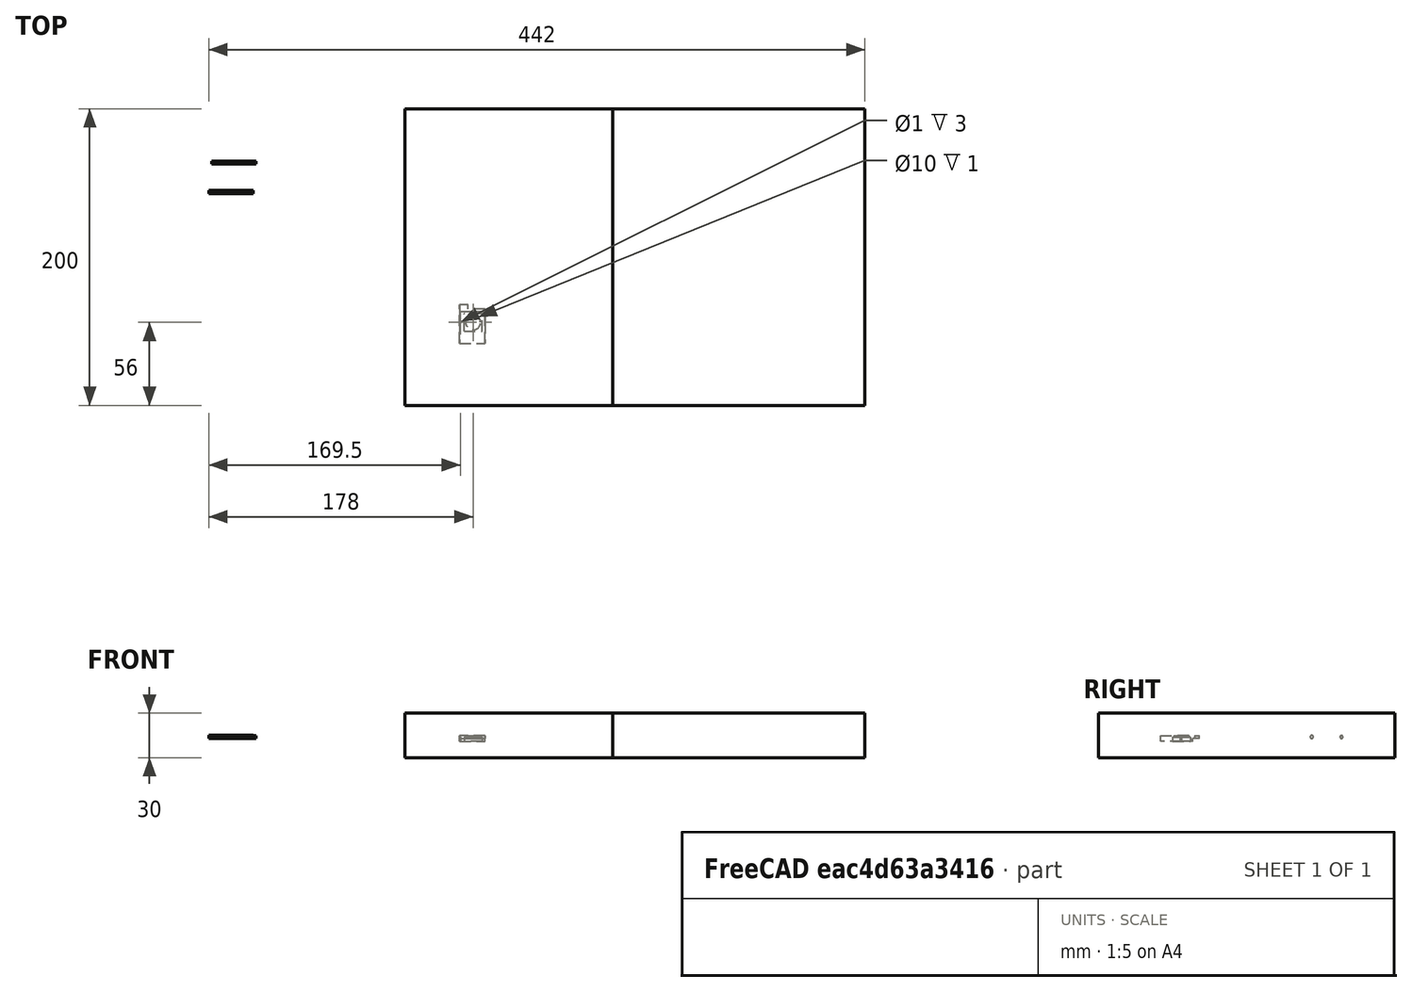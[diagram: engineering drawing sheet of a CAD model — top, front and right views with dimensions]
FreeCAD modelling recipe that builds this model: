
FCSTD DOCUMENT  (FreeCAD 0.17R13522 (Git))
Label: test_panel_2
License: CreativeCommons Attribution-ShareAlike
LicenseURL: http://creativecommons.org/licenses/by-sa/4.0/
objects: Part::Cut×39, Part::Feature×33, Part::Box×13, Part::Fuse×8, Part::Part2DObjectPython×7, Part::Cylinder×4, App::DocumentObjectGroup×3, Part::Extrusion×1
note: 105 computed .brp shape members not serialized (recipe doc carries the construction recipe); baked Part::Feature solids carry a one-line shape summary decoded from their .brp

FEATURE [Part::Part2DObjectPython] Line009  # Draft 2D object (typed FeaturePython)
  ChamferSize = 0
  Closed = false
  End = (270.847,20.2,0)
  FilletRadius = 0
  Length = 35.3471
  MakeFace = false
  Points = (2) [(235.5,20.2,0),(270.847,20.2,0)]
  Start = (235.5,20.2,0)
  Subdivisions = 0
FEATURE [Part::Part2DObjectPython] Circle001  # Draft 2D object (typed FeaturePython)
  FirstAngle = 0
  LastAngle = 0
  MakeFace = false
  Placement = pos=(259.67,20.2,0) rot=(0,0,1;0rad)
  Radius = 14
FEATURE [Part::Part2DObjectPython] Line014  # Draft 2D object (typed FeaturePython)
  ChamferSize = 0
  Closed = false
  End = (248.272,28.2144,0)
  FilletRadius = 0
  Length = 13.696
  MakeFace = false
  Placement = pos=(-10,0,-4) rot=(0,0,1;0rad)
  Points = (2) [(269.378,20.2,4),(258.272,28.2144,4)]
  Start = (259.378,20.2,0)
  Subdivisions = 0
FEATURE [Part::Part2DObjectPython] Line015  # Draft 2D object (typed FeaturePython)
  ChamferSize = 0
  Closed = false
  End = (254.876,33.263,0)
  FilletRadius = 0
  Length = 13.7518
  MakeFace = false
  Placement = pos=(-10,0,-4) rot=(0,0,1;0rad)
  Points = (2) [(269.174,20.2,4),(264.876,33.263,4)]
  Start = (259.174,20.2,0)
  Subdivisions = 0
FEATURE [Part::Part2DObjectPython] Line016  # Draft 2D object (typed FeaturePython)
  ChamferSize = 0
  Closed = false
  End = (263.227,33.6931,0)
  FilletRadius = 0
  Length = 14.1488
  MakeFace = false
  Placement = pos=(-10,0,-4) rot=(0,0,1;0rad)
  Points = (2) [(268.97,20.2,4),(273.227,33.6931,4)]
  Start = (258.97,20.2,0)
  Subdivisions = 0
FEATURE [Part::Part2DObjectPython] Line017  # Draft 2D object (typed FeaturePython)
  ChamferSize = 0
  Closed = false
  End = (270.612,28.9289,0)
  FilletRadius = 0
  Length = 14.5511
  MakeFace = false
  Placement = pos=(-10,0,-4) rot=(0,0,1;0rad)
  Points = (2) [(268.97,20.2,4),(280.612,28.9289,4)]
  Start = (258.97,20.2,0)
  Subdivisions = 0
FEATURE [App::DocumentObjectGroup] Construction
  Group = -> [Line009,Circle001,Line014,Line015,Line016,Line017]
FEATURE [Part::Box] Box001  label="Cube"
  AttacherType = Attacher::AttachEngine3D
  Height = 3
  Length = 6
  Placement = pos=(39,81,-108) rot=(0,0,1;0rad)
  Width = 6
FEATURE [Part::Feature] Fusion008001001061001  label="panel_siplays_encoders_dobles_y_spacers"
  Placement = pos=(0,0,-105) rot=(0,0,1;0rad)
  shape: bbox 280 x 210 x 10 mm, 411 faces (baked)
FEATURE [Part::Feature] Fusion003002001  label="el perforador001"
  Placement = pos=(48,115,-108) rot=(0,1,0;3.14159rad)
  shape: bbox 22 x 12 x 18 mm, 19 faces (baked)
FEATURE [Part::Feature] Fusion003002001001  label="el perforador002"
  Placement = pos=(87.5,115,-108) rot=(0,1,0;3.14159rad)
  shape: bbox 22 x 12 x 18 mm, 19 faces (baked)
FEATURE [Part::Cut] Cut001001001002003001008002002004
  Base = -> Fusion008001001061001
  Refine = true
  Tool = -> Fusion003002001
FEATURE [Part::Feature] Fusion003002001001001  label="el perforador003"
  Placement = pos=(127,115,-108) rot=(0,1,0;3.14159rad)
  shape: bbox 22 x 12 x 18 mm, 19 faces (baked)
FEATURE [Part::Cut] Cut001001001002003001008002002005
  Base = -> Cut001001001002003001008002002004
  Refine = true
  Tool = -> Fusion003002001001
FEATURE [Part::Feature] Fusion003002001001001001  label="el perforador004"
  Placement = pos=(166.5,115,-108) rot=(0,1,0;3.14159rad)
  shape: bbox 22 x 12 x 18 mm, 19 faces (baked)
FEATURE [Part::Feature] Fusion003002001001001001001  label="el perforador005"
  Placement = pos=(206,115,-108) rot=(0,1,0;3.14159rad)
  shape: bbox 22 x 12 x 18 mm, 19 faces (baked)
FEATURE [Part::Cut] Cut001001001002003001008002002006
  Base = -> Cut001001001002003001008002002005
  Refine = true
  Tool = -> Fusion003002001001001001
FEATURE [Part::Cut] Cut001001001002003001008002002007
  Base = -> Cut001001001002003001008002002006
  Refine = true
  Tool = -> Fusion003002001001001001001
FEATURE [Part::Feature] Fusion003002001001001001002001001  label="el perforador008"
  Placement = pos=(127,40,-108) rot=(0,1,0;3.14159rad)
  shape: bbox 22 x 12 x 18 mm, 19 faces (baked)
FEATURE [Part::Feature] Fusion003002001001001001002001002  label="el perforador009"
  Placement = pos=(127,80.5,-108) rot=(0,1,0;3.14159rad)
  shape: bbox 22 x 12 x 18 mm, 19 faces (baked)
FEATURE [Part::Feature] Fusion003002001001001001002001  label="el perforador007"
  Placement = pos=(127,55,-108) rot=(0,1,0;3.14159rad)
  shape: bbox 22 x 12 x 18 mm, 19 faces (baked)
FEATURE [Part::Feature] Fusion003002001001001001002  label="el perforador006"
  Placement = pos=(127,95.5,-108) rot=(0,1,0;3.14159rad)
  shape: bbox 22 x 12 x 18 mm, 19 faces (baked)
FEATURE [Part::Cut] Cut001001001002003001008002002008
  Base = -> Cut001001001002003001008002002007
  Refine = true
  Tool = -> Fusion003002001001001
FEATURE [Part::Cut] Cut001001001002003001008002002009
  Base = -> Cut001001001002003001008002002008
  Refine = true
  Tool = -> Fusion003002001001001001002
FEATURE [Part::Cut] Cut001001001002003001008002002010
  Base = -> Cut001001001002003001008002002009
  Refine = true
  Tool = -> Fusion003002001001001001002001
FEATURE [Part::Box] Box001001002002002001003001001004001001001001001001002  label="Cube034"
  AttacherType = Attacher::AttachEngine3D
  Height = 4
  Length = 32
  Placement = pos=(200,15,-108) rot=(0,0,1;0rad)
  Width = 10
FEATURE [Part::Fuse] Fusion003002001001001001002001003
  Base = -> Cut001001001002003001008002002010
  Refine = true
  Tool = -> Box001001002002002001003001001004001001001001001001002
FEATURE [Part::Fuse] Fusion003002001001001001002001004
  Base = -> Box001001002002002001003001001004001001001001001001002
  Refine = true
  Tool = -> Fusion003002001001001001002001003
FEATURE [Part::Fuse] Fusion003002001001001001002001005
  Refine = true
  Tool = -> Fusion003002001001001001002001004
FEATURE [Part::Fuse] Fusion003002001001001001002001006
  Base = -> Box001
  Refine = true
  Tool = -> Fusion003002001001001001002001005
FEATURE [Part::Feature] Fusion003002001001001001002001002001  label="el perforador010"
  Placement = pos=(47,80.5,-108) rot=(0,1,0;3.14159rad)
  shape: bbox 22 x 12 x 18 mm, 19 faces (baked)
FEATURE [Part::Feature] Fusion003002001001001001002001002002  label="el perforador011"
  Placement = pos=(87,80.5,-108) rot=(0,1,0;3.14159rad)
  shape: bbox 22 x 12 x 18 mm, 19 faces (baked)
FEATURE [Part::Feature] Fusion003002001001001001002001001001  label="el perforador012"
  Placement = pos=(87,40,-108) rot=(0,1,0;3.14159rad)
  shape: bbox 22 x 12 x 18 mm, 19 faces (baked)
FEATURE [Part::Feature] Fusion003002001001001001002001001001001  label="el perforador013"
  Placement = pos=(47,40,-108) rot=(0,1,0;3.14159rad)
  shape: bbox 22 x 12 x 18 mm, 19 faces (baked)
FEATURE [Part::Cut] Cut001001001002003001008002002011
  Base = -> Fusion003002001001001001002001006
  Refine = true
  Tool = -> Fusion003002001001001001002001002
FEATURE [Part::Cut] Cut001001001002003001008002002012
  Base = -> Cut001001001002003001008002002011
  Refine = true
  Tool = -> Fusion003002001001001001002001002002
FEATURE [Part::Cut] Cut001001001002003001008002002013
  Base = -> Cut001001001002003001008002002012
  Refine = true
  Tool = -> Fusion003002001001001001002001002001
FEATURE [Part::Cut] Cut001001001002003001008002002014
  Base = -> Cut001001001002003001008002002013
  Refine = true
  Tool = -> Fusion003002001001001001002001001001001
FEATURE [Part::Feature] Fusion003002001001001001002001001001002  label="el perforador014"
  Placement = pos=(220,8,-108) rot=(0.707107,0.707107,0;3.14159rad)
  shape: bbox 12 x 22 x 18 mm, 19 faces (baked)
FEATURE [Part::Cut] Cut001001001002003001008002002015
  Base = -> Cut001001001002003001008002002014
  Refine = true
  Tool = -> Fusion003002001001001001002001001001
FEATURE [Part::Cut] Cut001001001002003001008002002016
  Base = -> Cut001001001002003001008002002015
  Refine = true
  Tool = -> Fusion003002001001001001002001001
FEATURE [Part::Cut] Cut001001001002003001008002002017  label="base solo faltan los leds"
  Base = -> Cut001001001002003001008002002016
  Refine = true
  Tool = -> Fusion003002001001001001002001001001002
FEATURE [Part::Feature] Fusion001001  label="perforador led 3 mm001 rojo com2"
  Placement = pos=(24,43,-108) rot=(0,1,0;3.14159rad)
  shape: bbox 6 x 6 x 10 mm, 13 faces (baked)
FEATURE [Part::Feature] Fusion003002001001001001002001001001003  label="perforador led 3 mm002 rojo nav2"
  Placement = pos=(61,43,-108) rot=(0,1,0;3.14159rad)
  shape: bbox 6 x 6 x 10 mm, 13 faces (baked)
FEATURE [Part::Feature] Fusion003002001001001001002001001001004  label="perforador led 3 mm002 rojo adf2"
  Placement = pos=(101,43,-108) rot=(0,1,0;3.14159rad)
  shape: bbox 6 x 6 x 10 mm, 13 faces (baked)
FEATURE [Part::Feature] Fusion003002001001001001002001001001005  label="perforador led 3 mm001 rojo com1"
  Placement = pos=(24,83.5,-108) rot=(0,1,0;3.14159rad)
  shape: bbox 6 x 6 x 10 mm, 13 faces (baked)
FEATURE [Part::Feature] Fusion003002001001001001002001001001006  label="perforador led 3 mm002 rojo nav1"
  Placement = pos=(61,83.5,-108) rot=(0,1,0;3.14159rad)
  shape: bbox 6 x 6 x 10 mm, 13 faces (baked)
FEATURE [Part::Feature] Fusion003002001001001001002001001001007  label="perforador led 3 mm002 rojo adf1"
  Placement = pos=(101,83.5,-108) rot=(0,1,0;3.14159rad)
  shape: bbox 6 x 6 x 10 mm, 13 faces (baked)
FEATURE [Part::Cut] Cut
  Base = -> Cut001001001002003001008002002017
  Refine = true
  Tool = -> Fusion003002001001001001002001001001005
FEATURE [Part::Cut] Cut001001001002003001008002002018
  Base = -> Cut
  Refine = true
  Tool = -> Fusion003002001001001001002001001001006
FEATURE [Part::Cut] Cut001001001002003001008002002019
  Base = -> Cut001001001002003001008002002018
  Refine = true
  Tool = -> Fusion003002001001001001002001001001007
FEATURE [Part::Cut] Cut001001001002003001008002002020
  Base = -> Cut001001001002003001008002002019
  Refine = true
  Tool = -> Fusion003002001001001001002001001001004
FEATURE [Part::Cut] Cut001001001002003001008002002021
  Base = -> Cut001001001002003001008002002020
  Refine = true
  Tool = -> Fusion003002001001001001002001001001003
FEATURE [Part::Cut] Cut001001001002003001008002002022
  Base = -> Cut001001001002003001008002002021
  Refine = true
  Tool = -> Fusion001001
FEATURE [Part::Feature] Fusion003002001001001001002001001001008  label="perforador led 5 mm sound marker"
  Placement = pos=(40.75,133,-108) rot=(0,1,0;3.14159rad)
  shape: bbox 7.5 x 7.5 x 10 mm, 13 faces (baked)
FEATURE [Part::Feature] Fusion003002001001001001002001001001009  label="perforador led 5 mm sound com1"
  Placement = pos=(80.25,133,-108) rot=(0,1,0;3.14159rad)
  shape: bbox 7.5 x 7.5 x 10 mm, 13 faces (baked)
FEATURE [Part::Feature] Fusion003002001001001001002001001001010  label="perforador led 5 mm sound nav1"
  Placement = pos=(119.75,133,-108) rot=(0,1,0;3.14159rad)
  shape: bbox 7.5 x 7.5 x 10 mm, 13 faces (baked)
FEATURE [Part::Feature] Fusion003002001001001001002001001001011  label="perforador led 5 mm sound dme"
  Placement = pos=(159.25,133,-108) rot=(0,1,0;3.14159rad)
  shape: bbox 7.5 x 7.5 x 10 mm, 13 faces (baked)
FEATURE [Part::Feature] Fusion003002001001001001002001001001012  label="perforador led 5 mm sound adf1"
  Placement = pos=(198.75,133,-108) rot=(0,1,0;3.14159rad)
  shape: bbox 7.5 x 7.5 x 10 mm, 13 faces (baked)
FEATURE [Part::Feature] Fusion003002001001001001002001001001013  label="perforador led 5 mm ON/OFF"
  Placement = pos=(263.5,133,-108) rot=(0,1,0;3.14159rad)
  shape: bbox 7.5 x 7.5 x 10 mm, 13 faces (baked)
FEATURE [Part::Cut] Cut001001001002003001008002002023
  Base = -> Cut001001001002003001008002002022
  Refine = true
  Tool = -> Fusion003002001001001001002001001001013
FEATURE [Part::Cut] Cut001001001002003001008002002024
  Base = -> Cut001001001002003001008002002023
  Refine = true
  Tool = -> Fusion003002001001001001002001001001012
FEATURE [Part::Cut] Cut001001001002003001008002002025
  Base = -> Cut001001001002003001008002002024
  Refine = true
  Tool = -> Fusion003002001001001001002001001001011
FEATURE [Part::Cut] Cut001001001002003001008002002026
  Base = -> Cut001001001002003001008002002025
  Refine = true
  Tool = -> Fusion003002001001001001002001001001010
FEATURE [Part::Cut] Cut001001001002003001008002002027
  Base = -> Cut001001001002003001008002002026
  Refine = true
  Tool = -> Fusion003002001001001001002001001001009
FEATURE [Part::Cut] Cut001001001002003001008002002028
  Base = -> Cut001001001002003001008002002027
  Refine = true
  Tool = -> Fusion003002001001001001002001001001008
FEATURE [Part::Box] Box  label="Cube035"
  AttacherType = Attacher::AttachEngine3D
  Height = 10
  Length = 300
  Placement = pos=(-8,153.85,-111) rot=(0,0,1;0rad)
  Width = 120
FEATURE [Part::Cut] Cut001001001002003001008002002029  label="panel sin letras"
  Base = -> Cut001001001002003001008002002028
  Refine = true
  Tool = -> Box
FEATURE [Part::Box] Box001001002002002001003001001004001001001001001001003  label="cortador saca parte izquierda"
  AttacherType = Attacher::AttachEngine3D
  Height = 30
  Length = 140
  Placement = pos=(-10,-10,-119) rot=(0,0,1;0rad)
  Width = 200
FEATURE [Part::Box] Box001001002002002001003001001004001001001001001001004  label="cortador saca parte derecha"
  AttacherType = Attacher::AttachEngine3D
  Height = 30
  Length = 170
  Placement = pos=(130,-10,-119) rot=(0,0,1;0rad)
  Width = 200
FEATURE [Part::Cylinder] Cylinder  label="clavija agujereadora1_1"
  Angle = 360
  AttacherType = Attacher::AttachEngine3D
  Height = 30
  Placement = pos=(115,111.85,-106) rot=(0,1,0;1.5708rad)
  Radius = 1.05
FEATURE [Part::Cylinder] Cylinder001  label="clavija agujereadora2_1"
  Angle = 360
  AttacherType = Attacher::AttachEngine3D
  Height = 30
  Placement = pos=(115,37.85,-106) rot=(0,1,0;1.5708rad)
  Radius = 1.05
FEATURE [Part::Cylinder] Cylinder002  label="clavija empalmadora1"
  Angle = 360
  AttacherType = Attacher::AttachEngine3D
  Height = 29.8
  Placement = pos=(-140,153.85,-105) rot=(0,1,0;1.5708rad)
  Radius = 1
FEATURE [Part::Cut] Cut001001001002003001008002002030
  Base = -> Cut001001001002003001008002002029
  Refine = true
  Tool = -> Cylinder
FEATURE [Part::Cut] Cut001001001002003001008002002031  label="panel sin letras con agujeros clavijas"
  Base = -> Cut001001001002003001008002002030
  Refine = true
  Tool = -> Cylinder001
FEATURE [App::DocumentObjectGroup] Group  label="cortadores principales"
  Group = -> [Box001001002002002001003001001004001001001001001001003,Box001001002002002001003001001004001001001001001001004]
FEATURE [Part::Cylinder] Cylinder003  label="clavija hace agujero"
  Angle = 360
  AttacherType = Attacher::AttachEngine3D
  Height = 30
  Placement = pos=(-142,133.85,-105) rot=(0,1,0;1.5708rad)
  Radius = 1.05
FEATURE [App::DocumentObjectGroup] Group001  label="clavijas"
  Group = -> [Cylinder003,Cylinder002]
FEATURE [Part::Box] Box001001002002002001003001001004001001001001001001006  label="fleje abajo"
  AttacherType = Attacher::AttachEngine3D
  Height = 4
  Length = 280
  Placement = pos=(0,-4,-108) rot=(0,0,1;0rad)
  Width = 4
FEATURE [Part::Fuse] Fusion
  Base = -> Cut001001001002003001008002002031
  Refine = true
  Tool = -> Box001001002002002001003001001004001001001001001001006
FEATURE [Part::Feature] Cylinder002001  label="clavija empalmadora une frente base"
  Placement = pos=(30,-2,-134) rot=(0,0,1;1.5708rad)
  shape: bbox 2 x 2 x 29.8 mm, 3 faces (baked)
FEATURE [Part::Feature] Cylinder002001001  label="clavija empalmadora une frente base2"
  Placement = pos=(250,-2,-134) rot=(0,0,1;1.5708rad)
  shape: bbox 2 x 2 x 29.8 mm, 3 faces (baked)
FEATURE [Part::Fuse] Fusion003002001001001001002001001001014
  Base = -> Fusion
  Refine = true
  Tool = -> Cylinder002001
FEATURE [Part::Fuse] Fusion003002001001001001002001001001015  label="frente con clavijas sin letras"
  Base = -> Cylinder002001001
  Refine = true
  Tool = -> Fusion003002001001001001002001001001014
FEATURE [Part::Box] Box001001002002002001003001001004001001001001001001007  label="cortador clavijas"
  AttacherType = Attacher::AttachEngine3D
  Height = 4
  Length = 280
  Placement = pos=(0,0,-153) rot=(1,0,0;1.5708rad)
  Width = 30
FEATURE [Part::Cut] Cut001001001002003001008002002032  label="frente con clavijas de 15 sin letras"
  Base = -> Fusion003002001001001001002001001001015
  Refine = true
  Tool = -> Box001001002002002001003001001004001001001001001001007
FEATURE [Part::Box] Box001001002002002001003001001004001001001001001001008  label="Cube036"
  AttacherType = Attacher::AttachEngine3D
  Height = 1
  Length = 14
  Width = 14
FEATURE [Part::Part2DObjectPython] Circle002  # Draft 2D object (typed FeaturePython)
  FirstAngle = 0
  LastAngle = 0
  MakeFace = true
  Placement = pos=(7,7,1) rot=(0,0,1;3.14159rad)
  Radius = 5
FEATURE [Part::Extrusion] Extrude
  Base = -> Circle002
  Dir = (0,0,1)
  DirMode = 2
  FaceMakerClass = Part::FaceMakerBullseye
  LengthFwd = 10
  LengthRev = 0
  Placement = pos=(0,0,-6) rot=(0,0,1;0rad)
  Solid = false
  Symmetric = false
FEATURE [Part::Cut] Cut001001001002003001008002002033  label="circulo_para_botones"
  Base = -> Box001001002002002001003001001004001001001001001001008
  Placement = pos=(-28,0,0) rot=(0,0,1;0rad)
  Refine = true
  Tool = -> Extrude
FEATURE [Part::Feature] Cut001001001002003001008002002033001  label="circulo_para_botones001"
  Placement = pos=(29,39,-105) rot=(0,0,1;0rad)
  shape: bbox 14 x 14 x 1 mm, 7 faces (baked)
FEATURE [Part::Fuse] Fusion003002001001001001002001001001016
  Base = -> Cut001001001002003001008002002032
  Refine = true
  Tool = -> Cut001001001002003001008002002033001
FEATURE [Part::Box] Box001001002002002001003001001004001001001001001001009  label="Cube037"
  AttacherType = Attacher::AttachEngine3D
  Height = 60
  Length = 300
  Placement = pos=(44,-31,-120) rot=(0,0,1;0rad)
  Width = 250
FEATURE [Part::Cut] Cut001001001002003001008002002033002
  Base = -> Fusion003002001001001001002001001001016
  Refine = true
  Tool = -> Box001001002002002001003001001004001001001001001001009
FEATURE [Part::Box] Box001001002002002001003001001004001001001001001001010  label="Cube038"
  AttacherType = Attacher::AttachEngine3D
  Height = 10
  Length = 50
  Placement = pos=(-23,-26,-113) rot=(0,0,1;0rad)
  Width = 300
FEATURE [Part::Box] Box001001002002002001003001001004001001001001001001011  label="Cube039"
  AttacherType = Attacher::AttachEngine3D
  Height = 10
  Length = 58
  Placement = pos=(8,58,-107) rot=(0,0,1;0rad)
  Width = 150
FEATURE [Part::Cut] Cut001001001002003001008002002033003
  Base = -> Cut001001001002003001008002002033002
  Refine = true
  Tool = -> Box001001002002002001003001001004001001001001001001010
FEATURE [Part::Cut] Cut001001001002003001008002002033004
  Base = -> Cut001001001002003001008002002033003
  Refine = true
  Tool = -> Box001001002002002001003001001004001001001001001001011
FEATURE [Part::Box] Box001001002002002001003001001004001001001001001001012  label="Cube040"
  AttacherType = Attacher::AttachEngine3D
  Height = 200
  Length = 60
  Placement = pos=(-36,-18,-136) rot=(0,0,1;0rad)
  Width = 250
FEATURE [Part::Feature] Box001001002002002001003001001004001001001001001001012001  label="Cube041"
  Placement = pos=(200,-27,-136) rot=(0,0,1;0rad)
  shape: bbox 60 x 250 x 60 mm, 6 faces (baked)
FEATURE [Part::Feature] Box001001002002002001003001001004001001001001001001012002  label="Cube042"
  Placement = pos=(-2,-218,-136) rot=(0,0,1;0rad)
  shape: bbox 60 x 250 x 60 mm, 6 faces (baked)
FEATURE [Part::Feature] Box001001002002002001003001001004001001001001001001012003  label="Cube043"
  Placement = pos=(-5,60,-136) rot=(0,0,1;0rad)
  shape: bbox 60 x 250 x 60 mm, 6 faces (baked)
FEATURE [Part::Cut] Cut001001001002003001008002002033005
  Base = -> Cut001001001002003001008002002033
  Refine = true
  Tool = -> Box001001002002002001003001001004001001001001001001012
FEATURE [Part::Cut] Cut001001001002003001008002002033006
  Base = -> Cut001001001002003001008002002033004
  Refine = true
  Tool = -> Box001001002002002001003001001004001001001001001001012003
FEATURE [Part::Cut] Cut001001001002003001008002002033007
  Base = -> Cut001001001002003001008002002033006
  Refine = true
  Tool = -> Box001001002002002001003001001004001001001001001001012001
FEATURE [Part::Cut] Cut001001001002003001008002002033008
  Base = -> Cut001001001002003001008002002033007
  Refine = true
  Tool = -> Box001001002002002001003001001004001001001001001001012002
FEATURE [Part::Box] Box001001002002002001003001001004001001001001001001012004  label="Cube044"
  AttacherType = Attacher::AttachEngine3D
  Height = 60
  Length = 60
  Placement = pos=(-36,12,-150) rot=(0,0,1;0rad)
  Width = 60
FEATURE [Part::Cut] Cut001001001002003001008002002033009
  Base = -> Cut001001001002003001008002002033008
  Refine = true
  Tool = -> Box001001002002002001003001001004001001001001001001012004
